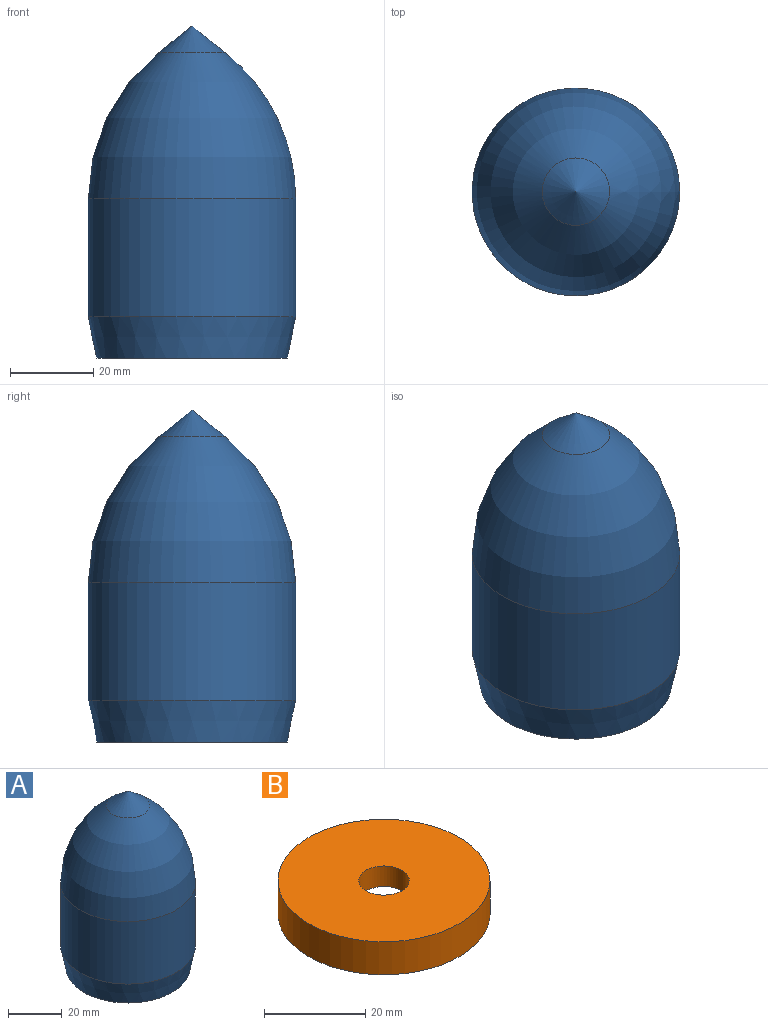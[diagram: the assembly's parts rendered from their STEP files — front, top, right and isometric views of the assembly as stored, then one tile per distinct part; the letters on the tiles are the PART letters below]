
ASSEMBLY  parts=2 mates=1
PART A: 10 faces, bbox 50x50x80 mm
  f0: cone r=8.11mm half-angle=51.3deg, axis (0,0,-1), area 264.7mm2, adj f1
  f1: revolved ~50x50mm, area 4868.3mm2, adj f0,f2
  f2: cylinder r=25mm len=50mm, axis (0,0,1), area 4456.6mm2, adj f1,f4
  f3: plane 46x46mm, normal (0,0,-1), area 276.5mm2, adj f4,f7
  f4: cone r=25mm half-angle=11.3deg, axis (0,0,1), area 1537.8mm2, adj f2,f3
  f5: cylinder r=19mm len=38mm, axis (0,0,-1), area 3129mm2, adj f6,f9
  f6: plane 42x42mm, normal (0,0,-1), area 251.3mm2, adj f5,f7
  f7: cylinder r=21mm len=42mm, axis (0,0,-1), area 1055.6mm2, adj f3,f6
  f8: cone r=3.11mm half-angle=51.3deg, axis (0,0,-1), area 39mm2, adj f9
  f9: revolved ~38x38mm, area 3231.2mm2, adj f5,f8
PART B: 6 faces, bbox 42x42x8 mm
  f0: plane 42x42mm, normal (0,0,-1), area 128.8mm2, adj f2,f5
  f1: plane 42x42mm, normal (0,0,1), area 1306.9mm2, adj f2,f3
  f2: cylinder r=21mm len=42mm, axis (0,0,-1), area 1055.6mm2, adj f0,f1
  f3: cylinder r=5mm len=10mm, axis (0,0,-1), area 157.1mm2, adj f1,f4
  f4: plane 34x34mm, normal (0,0,-1), area 829.4mm2, adj f3,f5
  f5: cone r=20mm half-angle=45deg, axis (0,0,-1), area 493.2mm2, adj f0,f4
PLACE A t=(0.08,-0.04,-27.62)mm
PLACE B t=(0.08,-0.04,-27.62)mm
MATE fastened B.f2 <-> A.f8  axis (0,0,1) through (0.08,-0.04,-19.62)mm
